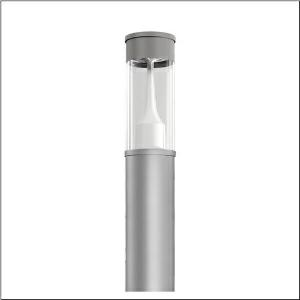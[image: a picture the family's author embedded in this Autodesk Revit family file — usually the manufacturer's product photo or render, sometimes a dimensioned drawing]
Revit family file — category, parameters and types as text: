
# Revit family: city-light_400_iq___st1_2a_5xa5305ef14hp_9457
name_source: partatom
category: Lighting Fixtures
units: mm (PartAtom-declared; Revit-internal decimal feet)

## family parameters
Cut with Voids When Loaded = No
Host = Face
Light Source = No
Part Type = Normal
Room Calculation Point = No
Round Connector Dimension = Use Diameter
Shared = No

## types (1)
- --- (1 x LED, 4730 lm, 33.6 W, 3000K)
    Apparent Load = 34 VA
    CIE Flux Codes = 22 61 94 96 100
    Color Rendering = 70
    Color Temperature = 3000K
    Default Elevation = 1800 mm
    Description = City-Light 400 iQ, light pillar, Module 540 iQ-SR, primary light control with 3 zone facetted reflector, of plastic, silver coated, highly specular, structured, primary optical cover: cover, of PMMA, transparent, partly coated, light distribution: ST1.2a, primary light characteristic: asymmetric, LED, High Power LED, rated luminous flux: 4.730lm, luminous efficacy: 141lm/W, light colour: 730, colour temperature: 3000K, control gear: ECG iQ, control: presetting dimming logarithmic, Street-Remote, Auto-Match, Temp-Guard, Lumen-Switch, Night-Set, Smart-Wire, Light-Fading, Desk-Remote (wireless, voltage-free reading and setting of iQ features in the workshop via application-optimized NFC function/RFID function), optimised constant luminous flux control (CLO 2.0), with terminal, 6-pole, max. 2.5mm², mains connection: 230..240V, AC, 50/60Hz, start of lifetime: 34W, end of service life: 36W, reduction: 15W, luminaire housing, cylindrical, of extruded aluminium section, coated, Siteco® metallic grey (DB 702S), length: 4.694mm, diameter: 200mm, Module 540 iQ-SR, traffic white (RAL 9016), equipment: Power, protection rating (complete): IP65, insulation class (complete): insulation class II (safety insulation), certification: CE, ENEC, VDE, packaging unit: 1 piece

Light Distribution: ST1.2a
    Height = 500 mm
    Lamp = 1 x LED
    Lamp Light Flux = 4730 lm
    Lamp Power = 33.6 W
    Lamp count = 1
    Length = 200 mm  [stored 0.656168 ft]
    Luminous efficacy = 141 lm/W
    Manufacturer = Siteco
    ModVariant = No
    Model = 5XA5305EF14HP
    Mounting Place = Floor
    Mounting Type = Freestanding
    Number of Poles = 1
    OnlyDefault = Yes
    Power Factor = 1
    Product Name = City-Light 400 iQ | ST1.2a
    Product group = light pillar
    ProductGroupID = 1303
    Protection Class = Protection class II
    Protection Degree = IP 65
    RLX_Detail_Level = 1
    RLX_Emergency_Light_Flux = 0 lm
    RLX_Emergency_Type = 0
    RLX_Emergency_Type_DB = No
    RlxData = <blob elided: 53557 chars, md5=f101611e>
    Socket = socket
    Standby Power = 0 W
    System Light Flux = 4730 lm
    System Power = 34 W
    Type Comments = factory setting: luminous flux: 100 % | dim-lin: 254 | 695 mA
    Type Image = l_1006916.jpg
    URL = http://relux.com
    VarID = @adj_145505
    Voltage = 0 V
    Weight = 0.00 kg
    Width = 0 mm  [stored 0 ft]

note: [stored X ft] marks values corroborated as IEEE doubles in the binary element streams (Revit-internal decimal feet)

## geometry (parser evidence)
native form markers: Blend x4, Sweep x11
no freeform markers — native parametric forms only
